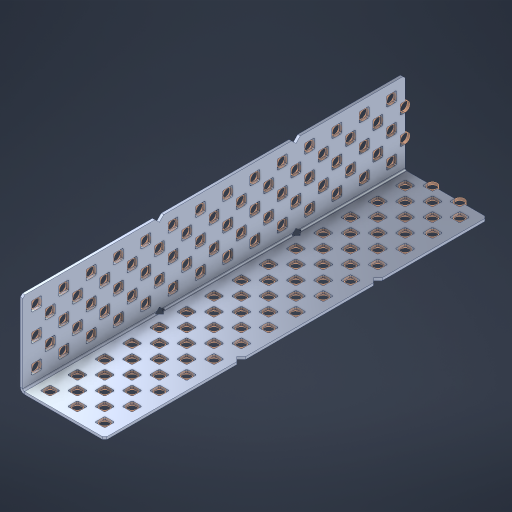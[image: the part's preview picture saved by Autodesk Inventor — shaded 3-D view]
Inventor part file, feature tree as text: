
AUTODESK INVENTOR PART (.ipt)
format: ipt  version: 2023 (Build 270158000, 158)  size: 1,658,880 bytes
history: native  units: in
note: dims shown in document units (in); Inventor stores cm internally (conversion verified against a paired STEP export)
features: other x146, extrude x138, sheet_metal_op x8, sketch x7, pattern_linear x3, mirror x1, chamfer x1
ambient origin geometry x8: Origin, YZ Plane, XZ Plane, XY Plane, X Axis, Y Axis, Z Axis, Center Point
bodies: Solid1 (feature_tree), Body (feature_tree)
feature tree (304):
  sheet_metal_op  "Flanges"
  sheet_metal_op  "Body Pattern"
  pattern_linear  "Center Double"  Spacing1=1.5in  [1 undecoded]
  pattern_linear  "Center Pattern"  Spacing1=0.1875in  [1 undecoded]
  other  "Arc Length"
  pattern_linear  "Notch Pattern"  Spacing1=0.0469in  [1 undecoded]
  other  "Diagonal Plane"
  mirror  "Everything Mirrored"
  chamfer  "End Chamfer"
  sketch  "Sketch1"  dims[d0=1.5in]
  other  "Plate1"
  sketch  "Sketch2"  dims[d1=7.0in]
  other  "Plate2"
  sheet_metal_op  "Bend1"
  sheet_metal_op  "Corner1"
  sketch  "Sketch8"  dims[d2=0.0469in]
  sketch  "Sketch9"  dims[d3=0.0469in]
  other  "Srf91"
  sheet_metal_op  "Body Pattern Sketch"
  other  "Srf92"
  sketch  "Sketch13"  dims[d4=0.0234in]
  sketch  "Sketch15"  dims[d5=0.0938in]
  sketch  "Sketch16"  dims[d6=0.0469in d7=1.5in d8=90.0deg d9=0.0312in d10=0.1875in d11=0.0469in d12=0.0469in d49=0.182in d50=0.02in d52=0.25in d53=0.0469in d54=0.0in d55=0.172in d56=1.0in d57=0.0in d85=0.1473in d86=0.1659in d89=0.0469in d90=0.0in d91=0.04in d92=0.0491in d95=2.5in d96=0.04in d97=0.25in d98=45.0deg d106=0.182in d107=0.02in d110=0.0469in d111=0.0in d112=0.172in d113=0.5in d114=0.0in d117=0.5in d126=0.0491in d127=0.1227in d128=0.08in d129=0.04in d130=2.5in d131=0.25in d132=5.5118in d134=0.5in d135=1.1811in d137=0.5in d140=0.5in d141=1.0in d142=0.3937in d144=0.5in d145=0.071in d146=0.7874in d148=0.5in]
  other  "Srf786"
  other  "Srf856"
  other  "Srf889"
  other  "Srf890"
  other  "Srf891"
  other  "Srf1275"
  other  "Srf1276"
  other  "Srf1278"
  other  "Srf1277"
  other  "Srf1285"
  other  "Srf1286"
  other  "Srf1287"
  other  "Srf1445"
  other  "Srf1446"
  other  "Srf1447"
  other  "Srf1448"
  other  "Srf1449"
  other  "Srf1537"
  other  "Srf1538"
  other  "Srf1539"
  other  "Srf1540"
  other  "Srf1541"
  other  "Srf1807"
  other  "Srf1808"
  other  "Srf1809"
  other  "Srf1810"
  other  "Srf1811"
  other  "Srf1959"
  other  "Srf1960"
  other  "Srf1961"
  other  "Srf1962"
  other  "Srf1963"
  other  "Srf2009"
  other  "Srf2010"
  other  "Srf2011"
  other  "Srf2012"
  other  "Srf2013"
  other  "Srf2014"
  other  "Srf2015"
  other  "Srf2016"
  other  "Srf2017"
  other  "Srf2018"
  other  "Srf2019"
  other  "Srf2020"
  other  "Srf2021"
  other  "Srf2022"
  other  "Srf2043"
  other  "Srf2044"
  other  "Srf2045"
  other  "Srf2046"
  other  "Srf2047"
  other  "Srf2048"
  other  "Srf2049"
  other  "Srf2050"
  other  "Srf2051"
  other  "Srf2052"
  other  "Srf2053"
  other  "Srf2054"
  other  "Srf2055"
  other  "Srf2076"
  other  "Srf2077"
  other  "Srf2078"
  other  "Srf2079"
  other  "Srf2080"
  other  "Srf2081"
  other  "Srf2082"
  other  "Srf2083"
  other  "Srf2084"
  other  "Srf2085"
  other  "Srf2086"
  other  "Srf2087"
  other  "Srf2088"
  other  "Srf2089"
  other  "Srf2090"
  other  "Srf2091"
  other  "Srf2092"
  other  "Srf2093"
  other  "Srf2094"
  other  "Srf2095"
  other  "Srf2096"
  other  "Srf2097"
  other  "Srf2098"
  other  "Srf2099"
  other  "Srf2100"
  other  "Srf2101"
  other  "Srf2102"
  other  "Srf2103"
  other  "Srf2104"
  other  "Srf2105"
  other  "Srf2106"
  other  "Srf2107"
  other  "Srf2108"
  other  "Srf2109"
  other  "Srf2110"
  other  "Srf2111"
  other  "Srf2112"
  other  "Srf2113"
  other  "Srf2114"
  other  "Srf2115"
  other  "Srf2179"
  other  "Srf2180"
  other  "Srf2181"
  other  "Srf2182"
  other  "Srf2183"
  other  "Srf2184"
  other  "Srf2185"
  other  "Srf2186"
  other  "Srf2187"
  other  "Srf2188"
  other  "Srf2189"
  other  "Srf2190"
  other  "Srf2191"
  other  "Srf2192"
  other  "Srf2193"
  other  "Srf2194"
  other  "Srf2195"
  other  "Srf2196"
  other  "Srf2197"
  other  "Srf2198"
  other  "Srf2199"
  other  "Srf2200"
  other  "Srf2201"
  other  "Srf2202"
  other  "Srf2203"
  other  "Srf2204"
  other  "Srf2205"
  other  "Srf2206"
  other  "Srf2207"
  other  "Srf2208"
  other  "Srf2209"
  other  "Srf2210"
  other  "Srf2211"
  other  "Srf2212"
  other  "Srf2213"
  other  "Srf2214"
  other  "Srf2215"
  other  "Srf2216"
  other  "Srf2217"
  sheet_metal_op  "Body Stamp"
  sheet_metal_op  "Body Circle"
  other  "Center Stamp"
  other  "Center Circle"
  sheet_metal_op  "Notch"
  extrude  "ExtrusionSrf92"  Depth=0.0469in
  extrude  "ExtrusionSrf856"  Depth=0.182in
  extrude  "ExtrusionSrf889"  Depth=0.02in
  extrude  "ExtrusionSrf890"  Depth=0.25in
  extrude  "ExtrusionSrf891"  Depth=0.0469in
  extrude  "ExtrusionSrf1275"  TaperAngle=0.0deg  [1 undecoded]
  extrude  "ExtrusionSrf1276"  Depth=0.5in
  extrude  "ExtrusionSrf1277"  Depth=1.0in TaperAngle=0.0deg
  extrude  "ExtrusionSrf1345"  Depth=0.5in
  extrude  "ExtrusionSrf1346"  Depth=0.5in
  extrude  "ExtrusionSrf1347"  Depth=0.0469in
  extrude  "ExtrusionSrf1348"  Depth=0.5in TaperAngle=0.0deg
  extrude  "ExtrusionSrf1445"  Depth=0.5in
  extrude  "ExtrusionSrf1446"  Depth=0.25in TaperAngle=45.0deg
  extrude  "ExtrusionSrf1447"  Depth=0.182in
  extrude  "ExtrusionSrf1448"  Depth=0.02in
  extrude  "ExtrusionSrf1449"  Depth=0.0469in
  extrude  "ExtrusionSrf1537"  TaperAngle=0.0deg  [1 undecoded]
  extrude  "ExtrusionSrf1538"  Depth=0.5in
  extrude  "ExtrusionSrf1539"  Depth=0.5in TaperAngle=0.0deg
  extrude  "ExtrusionSrf1540"  Depth=0.5in
  extrude  "ExtrusionSrf1541"  Depth=0.5in
  extrude  "ExtrusionSrf1807"  Depth=0.5in
  extrude  "ExtrusionSrf1808"  Depth=0.5in
  extrude  "ExtrusionSrf1809"  Depth=0.5in
  extrude  "ExtrusionSrf1810"  Depth=0.5in
  extrude  "ExtrusionSrf1811"  Depth=0.25in
  extrude  "ExtrusionSrf1959"  Depth=0.5in
  extrude  "ExtrusionSrf1960"  Depth=0.5in
  extrude  "ExtrusionSrf1961"  Depth=0.5in
  extrude  "ExtrusionSrf1962"  Depth=1.0in
  extrude  "ExtrusionSrf1963"  Depth=0.3937in
  extrude  "ExtrusionSrf2009"  Depth=0.5in
  extrude  "ExtrusionSrf2010"  Depth=0.5in
  extrude  "ExtrusionSrf2011"  [1 undecoded]
  extrude  "ExtrusionSrf2012"  [1 undecoded]
  extrude  "ExtrusionSrf2013"  [1 undecoded]
  extrude  "ExtrusionSrf2014"  [1 undecoded]
  extrude  "ExtrusionSrf2015"  [1 undecoded]
  extrude  "ExtrusionSrf2016"  [1 undecoded]
  extrude  "ExtrusionSrf2017"  [1 undecoded]
  extrude  "ExtrusionSrf2018"  [1 undecoded]
  extrude  "ExtrusionSrf2019"  [1 undecoded]
  extrude  "ExtrusionSrf2020"  [1 undecoded]
  extrude  "ExtrusionSrf2021"  [1 undecoded]
  extrude  "ExtrusionSrf2022"  [1 undecoded]
  extrude  "ExtrusionSrf2043"  [1 undecoded]
  extrude  "ExtrusionSrf2044"  [1 undecoded]
  extrude  "ExtrusionSrf2045"  [1 undecoded]
  extrude  "ExtrusionSrf2046"  [1 undecoded]
  extrude  "ExtrusionSrf2047"  [1 undecoded]
  extrude  "ExtrusionSrf2048"  [1 undecoded]
  extrude  "ExtrusionSrf2049"  [1 undecoded]
  extrude  "ExtrusionSrf2050"  [1 undecoded]
  extrude  "ExtrusionSrf2051"  [1 undecoded]
  extrude  "ExtrusionSrf2052"  [1 undecoded]
  extrude  "ExtrusionSrf2053"  [1 undecoded]
  extrude  "ExtrusionSrf2054"  [1 undecoded]
  extrude  "ExtrusionSrf2055"  [1 undecoded]
  extrude  "ExtrusionSrf2076"  [1 undecoded]
  extrude  "ExtrusionSrf2077"  [1 undecoded]
  extrude  "ExtrusionSrf2078"  [1 undecoded]
  extrude  "ExtrusionSrf2079"  [1 undecoded]
  extrude  "ExtrusionSrf2080"  [1 undecoded]
  extrude  "ExtrusionSrf2081"  [1 undecoded]
  extrude  "ExtrusionSrf2082"  [1 undecoded]
  extrude  "ExtrusionSrf2083"  [1 undecoded]
  extrude  "ExtrusionSrf2084"  [1 undecoded]
  extrude  "ExtrusionSrf2085"  [1 undecoded]
  extrude  "ExtrusionSrf2086"  [1 undecoded]
  extrude  "ExtrusionSrf2087"  [1 undecoded]
  extrude  "ExtrusionSrf2088"  [1 undecoded]
  extrude  "ExtrusionSrf2089"  [1 undecoded]
  extrude  "ExtrusionSrf2090"  [1 undecoded]
  extrude  "ExtrusionSrf2091"  [1 undecoded]
  extrude  "ExtrusionSrf2092"  [1 undecoded]
  extrude  "ExtrusionSrf2093"  [1 undecoded]
  extrude  "ExtrusionSrf2094"  [1 undecoded]
  extrude  "ExtrusionSrf2095"  [1 undecoded]
  extrude  "ExtrusionSrf2096"  [1 undecoded]
  extrude  "ExtrusionSrf2097"  [1 undecoded]
  extrude  "ExtrusionSrf2098"  [1 undecoded]
  extrude  "ExtrusionSrf2099"  [1 undecoded]
  extrude  "ExtrusionSrf2100"  [1 undecoded]
  extrude  "ExtrusionSrf2101"  [1 undecoded]
  extrude  "ExtrusionSrf2102"  [1 undecoded]
  extrude  "ExtrusionSrf2103"  [1 undecoded]
  extrude  "ExtrusionSrf2104"  [1 undecoded]
  extrude  "ExtrusionSrf2105"  [1 undecoded]
  extrude  "ExtrusionSrf2106"  [1 undecoded]
  extrude  "ExtrusionSrf2107"  [1 undecoded]
  extrude  "ExtrusionSrf2108"  [1 undecoded]
  extrude  "ExtrusionSrf2109"  [1 undecoded]
  extrude  "ExtrusionSrf2110"  [1 undecoded]
  extrude  "ExtrusionSrf2111"  [1 undecoded]
  extrude  "ExtrusionSrf2112"  [1 undecoded]
  extrude  "ExtrusionSrf2113"  [1 undecoded]
  extrude  "ExtrusionSrf2114"  [1 undecoded]
  extrude  "ExtrusionSrf2115"  [1 undecoded]
  extrude  "ExtrusionSrf2179"  [1 undecoded]
  extrude  "ExtrusionSrf2180"  [1 undecoded]
  extrude  "ExtrusionSrf2181"  [1 undecoded]
  extrude  "ExtrusionSrf2182"  [1 undecoded]
  extrude  "ExtrusionSrf2183"  [1 undecoded]
  extrude  "ExtrusionSrf2184"  [1 undecoded]
  extrude  "ExtrusionSrf2185"  [1 undecoded]
  extrude  "ExtrusionSrf2186"  [1 undecoded]
  extrude  "ExtrusionSrf2187"  [1 undecoded]
  extrude  "ExtrusionSrf2188"  [1 undecoded]
  extrude  "ExtrusionSrf2189"  [1 undecoded]
  extrude  "ExtrusionSrf2190"  [1 undecoded]
  extrude  "ExtrusionSrf2191"  [1 undecoded]
  extrude  "ExtrusionSrf2192"  [1 undecoded]
  extrude  "ExtrusionSrf2193"  [1 undecoded]
  extrude  "ExtrusionSrf2194"  [1 undecoded]
  extrude  "ExtrusionSrf2195"  [1 undecoded]
  extrude  "ExtrusionSrf2196"  [1 undecoded]
  extrude  "ExtrusionSrf2197"  [1 undecoded]
  extrude  "ExtrusionSrf2198"  [1 undecoded]
  extrude  "ExtrusionSrf2199"  [1 undecoded]
  extrude  "ExtrusionSrf2200"  [1 undecoded]
  extrude  "ExtrusionSrf2201"  [1 undecoded]
  extrude  "ExtrusionSrf2202"  [1 undecoded]
  extrude  "ExtrusionSrf2203"  [1 undecoded]
  extrude  "ExtrusionSrf2204"  [1 undecoded]
  extrude  "ExtrusionSrf2205"  [1 undecoded]
  extrude  "ExtrusionSrf2206"  [1 undecoded]
  extrude  "ExtrusionSrf2207"  [1 undecoded]
  extrude  "ExtrusionSrf2208"  [1 undecoded]
  extrude  "ExtrusionSrf2209"  [1 undecoded]
  extrude  "ExtrusionSrf2210"  [1 undecoded]
  extrude  "ExtrusionSrf2211"  [1 undecoded]
  extrude  "ExtrusionSrf2212"  [1 undecoded]
  extrude  "ExtrusionSrf2213"  [1 undecoded]
  extrude  "ExtrusionSrf2214"  [1 undecoded]
  extrude  "ExtrusionSrf2215"  [1 undecoded]
  extrude  "ExtrusionSrf2216"  [1 undecoded]
  extrude  "ExtrusionSrf2217"  [1 undecoded]
note: 109 required parameter values undecoded (feature->parameter linkage not recoverable at this tier; creation-order binding heuristic only, values carry confidence <= 0.55)
